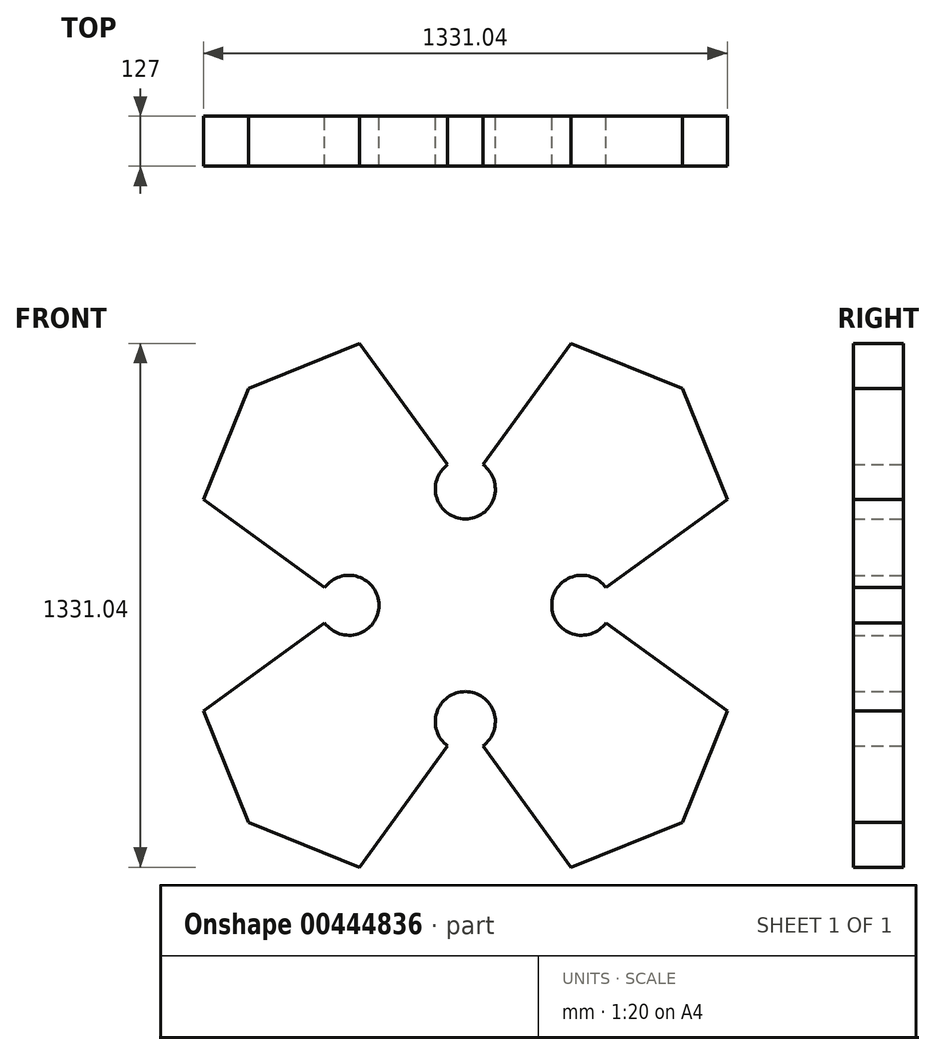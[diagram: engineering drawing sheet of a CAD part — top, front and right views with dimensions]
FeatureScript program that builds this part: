
annotation { "Feature Type Name" : "Feature", "Feature Type Description" : "" }
export const myFeature = defineFeature(function(context is Context, id is Id, definition is map)
    precondition{}
    {
        {
            var Q0;
            Q0=qCreatedBy(makeId("Front.planeOp"),FACE);
            var sketch = newSketch(context, id + "F0", { "sketchPlane" : qUnion([Q0])});
            skLineSegment(sketch, "E0", {"start": v(-449.01, -449.01) * mm, "end": v(-166.4, -563.2) * mm});
            skLineSegment(sketch, "E1", {"start": v(-166.4, -563.2) * mm, "end": v(57.54, -254.96) * mm});
            skLineSegment(sketch, "E2.MirrorCS", {"start": v(-449.01, -449.01) * mm, "end": v(-563.2, -166.4) * mm});
            skLineSegment(sketch, "E3.MirrorCS", {"start": v(-563.2, -166.4) * mm, "end": v(-254.96, 57.54) * mm});
            skLineSegment(sketch, "E4.1.0", {"start": v(-166.4, 767.85) * mm, "end": v(57.54, 459.61) * mm});
            skLineSegment(sketch, "E4.1.1", {"start": v(-449.01, 653.67) * mm, "end": v(-166.4, 767.85) * mm});
            skLineSegment(sketch, "E4.1.2", {"start": v(-449.01, 653.67) * mm, "end": v(-563.2, 371.06) * mm});
            skLineSegment(sketch, "E4.1.3", {"start": v(-563.2, 371.06) * mm, "end": v(-254.96, 147.12) * mm});
            skLineSegment(sketch, "E4.2.0", {"start": v(767.85, 371.06) * mm, "end": v(459.61, 147.12) * mm});
            skLineSegment(sketch, "E4.2.1", {"start": v(653.67, 653.67) * mm, "end": v(767.85, 371.06) * mm});
            skLineSegment(sketch, "E4.2.2", {"start": v(653.67, 653.67) * mm, "end": v(371.06, 767.85) * mm});
            skLineSegment(sketch, "E4.2.3", {"start": v(371.06, 767.85) * mm, "end": v(147.12, 459.61) * mm});
            skLineSegment(sketch, "E4.3.0", {"start": v(371.06, -563.2) * mm, "end": v(147.12, -254.96) * mm});
            skLineSegment(sketch, "E4.3.1", {"start": v(653.67, -449.01) * mm, "end": v(371.06, -563.2) * mm});
            skLineSegment(sketch, "E4.3.2", {"start": v(653.67, -449.01) * mm, "end": v(767.85, -166.4) * mm});
            skLineSegment(sketch, "E4.3.3", {"start": v(767.85, -166.4) * mm, "end": v(459.61, 57.54) * mm});
            skPoint(sketch, "E4.center", {"position": v(102.33, 102.33) * mm});
            skPoint(sketch, "E5.orphan", {"position": v(131.88, 357.29) * mm});
            skPoint(sketch, "E6.orphan", {"position": v(72.77, 357.29) * mm});
            skPoint(sketch, "E7.orphan", {"position": v(357.29, 131.88) * mm});
            skPoint(sketch, "E8.orphan", {"position": v(357.29, 72.77) * mm});
            skPoint(sketch, "E9.orphan", {"position": v(72.77, -152.63) * mm});
            skPoint(sketch, "E10.orphan", {"position": v(131.88, -152.63) * mm});
            skPoint(sketch, "E11.orphan", {"position": v(-152.63, 72.77) * mm});
            skPoint(sketch, "E12.orphan", {"position": v(-152.63, 131.88) * mm});
            skArc(sketch, "E13", {"start": v(57.54, 459.61) * mm, "mid": v(102.33, 321.77) * mm, "end": v(147.12, 459.61) * mm});
            skArc(sketch, "E14", {"start": v(459.61, 147.12) * mm, "mid": v(321.77, 102.33) * mm, "end": v(459.61, 57.54) * mm});
            skArc(sketch, "E15", {"start": v(147.12, -254.96) * mm, "mid": v(102.33, -117.11) * mm, "end": v(57.54, -254.96) * mm});
            skArc(sketch, "E16", {"start": v(-254.96, 57.54) * mm, "mid": v(-117.11, 102.33) * mm, "end": v(-254.96, 147.12) * mm});
            skSolve(sketch);
        }
        {
            var Q0;
            Q0=makeQuery(id+"F0.imprint","IMPRINT",FACE,{"disambiguationData":[TD([[makeQuery(id+"F0.imprint","IMPRINT",EDGE,{"derivedFrom":sQuery(id+"F0.wireOp",EDGE,"E0")}),1.0]])]});
            extrude(context, id + "F1", {"entities" : qUnion([Q0]), "depth" : 127 * mm});
        }
    });
